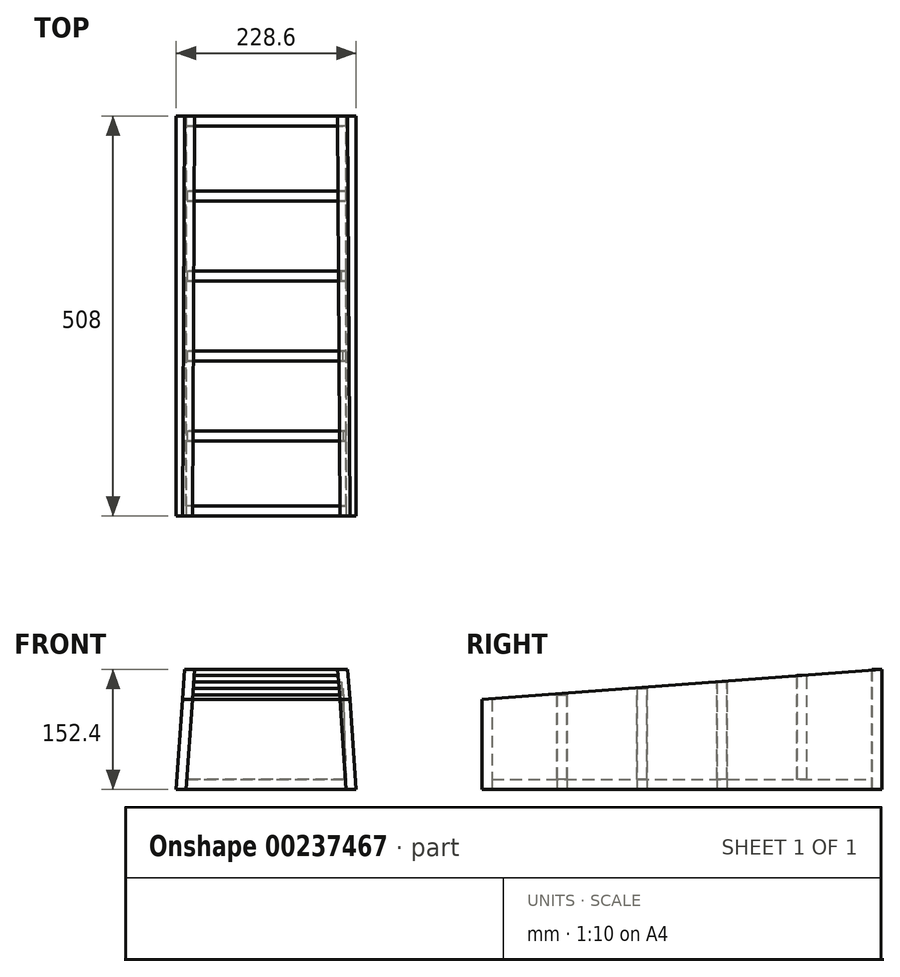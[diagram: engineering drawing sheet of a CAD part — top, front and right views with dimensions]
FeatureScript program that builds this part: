
annotation { "Feature Type Name" : "Feature", "Feature Type Description" : "" }
export const myFeature = defineFeature(function(context is Context, id is Id, definition is map)
    precondition{}
    {
        {
            var Q0;
            Q0=qCreatedBy(makeId("Right.planeOp"),FACE);
            var sketch = newSketch(context, id + "F0", { "sketchPlane" : qUnion([Q0])});
            skLineSegment(sketch, "E0", {"start": v(0, 0) * mm, "end": v(0, 152.4) * mm});
            skLineSegment(sketch, "E1", {"start": v(0, 152.4) * mm, "end": v(-508, 114.3) * mm});
            skLineSegment(sketch, "E2", {"start": v(-508, 114.3) * mm, "end": v(-508, 0) * mm});
            skLineSegment(sketch, "E3", {"start": v(-508, 0) * mm, "end": v(0, 0) * mm});
            skSolve(sketch);
        }
        {
            var Q0;
            Q0=makeQuery(id+"F0.imprint","IMPRINT",FACE,{"disambiguationData":[TD([[makeQuery(id+"F0.imprint","IMPRINT",EDGE,{"derivedFrom":sQuery(id+"F0.wireOp",EDGE,"E0")}),1.0]])]});
            extrude(context, id + "F1", {"entities" : qUnion([Q0]), "oppositeDirection" : true, "depth" : 114.3 * mm});
        }
        {
            var Q0;
            Q0=qCreatedBy(makeId("Front.planeOp"),FACE);
            var sketch = newSketch(context, id + "F2", { "sketchPlane" : qUnion([Q0])});
            skLineSegment(sketch, "E4", {"start": v(-114.3, 0) * mm, "end": v(-103.46, 155.08) * mm});
            skLineSegment(sketch, "E5", {"start": v(-103.46, 155.08) * mm, "end": v(-133.17, 155.08) * mm});
            skLineSegment(sketch, "E6", {"start": v(-133.17, 155.08) * mm, "end": v(-133.17, 0) * mm});
            skLineSegment(sketch, "E7", {"start": v(-133.17, 0) * mm, "end": v(-114.3, 0) * mm});
            skSolve(sketch);
        }
        {
            var Q0;
            Q0=makeQuery(id+"F2.imprint","IMPRINT",FACE,{"disambiguationData":[TD([[makeQuery(id+"F2.imprint","IMPRINT",EDGE,{"derivedFrom":sQuery(id+"F2.wireOp",EDGE,"E4")}),1.0]])]});
            var Q1;
            Q1=makeQuery(id+"F1.opExtrude","SWEPT_BODY",BODY,{"disambiguationData":[OSD([sQuery(id+"F0.wireOp",EDGE,"E0"),sQuery(id+"F0.wireOp",EDGE,"E1"),sQuery(id+"F0.wireOp",EDGE,"E2"),sQuery(id+"F0.wireOp",EDGE,"E3")])]});
            extrude(context, id + "F3", {"entities" : qUnion([Q0]), "operationType" : NewBodyOperationType.REMOVE, "endBoundEntityBody" : qUnion([Q1]), "depth" : 528.32 * mm});
        }
        {
            var Q0;
            Q0=qCreatedBy(makeId("Front.planeOp"),FACE);
            var sketch = newSketch(context, id + "F4", { "sketchPlane" : qUnion([Q0])});
            skLineSegment(sketch, "E8", {"start": v(-90.18, 162.83) * mm, "end": v(-102.71, -16.34) * mm});
            skLineSegment(sketch, "E9", {"start": v(-102.71, -16.34) * mm, "end": v(0, -16.34) * mm});
            skLineSegment(sketch, "E10", {"start": v(0, -16.34) * mm, "end": v(0, 168.36) * mm});
            skLineSegment(sketch, "E11", {"start": v(0, 168.36) * mm, "end": v(-90.18, 162.83) * mm});
            skSolve(sketch);
        }
        {
            var Q0;
            Q0=makeQuery(id+"F4.imprint","IMPRINT",FACE,{"disambiguationData":[TD([[makeQuery(id+"F4.imprint","IMPRINT",EDGE,{"derivedFrom":sQuery(id+"F4.wireOp",EDGE,"E8")}),1.0]])]});
            extrude(context, id + "F5", {"entities" : qUnion([Q0]), "operationType" : NewBodyOperationType.REMOVE, "depth" : 508 * mm});
        }
        {
            var Q0;
            Q0=makeQuery(id+"F1.opExtrude","SWEPT_BODY",BODY,{"disambiguationData":[OSD([sQuery(id+"F0.wireOp",EDGE,"E0"),sQuery(id+"F0.wireOp",EDGE,"E1"),sQuery(id+"F0.wireOp",EDGE,"E2"),sQuery(id+"F0.wireOp",EDGE,"E3")])]});
            var Q1;
            Q1=qCreatedBy(makeId("Right.planeOp"),FACE);
            mirror(context, id + "F6", {"entities" : qUnion([Q0]), "mirrorPlane" : qUnion([Q1])});
        }
        {
            var Q0;
            Q0=makeQuery(id+"F1.opExtrude","SWEPT_FACE",FACE,{"disambiguationData":[OSD([sQuery(id+"F0.wireOp",EDGE,"E0")])]});
            var sketch = newSketch(context, id + "F7", { "sketchPlane" : qUnion([Q0])});
            skLineSegment(sketch, "E12", {"start": v(-90.91, 152.4) * mm, "end": v(90.91, 152.4) * mm});
            skLineSegment(sketch, "E13", {"start": v(90.91, 152.4) * mm, "end": v(101.57, 0) * mm});
            skLineSegment(sketch, "E14", {"start": v(101.57, 0) * mm, "end": v(-101.57, 0) * mm});
            skLineSegment(sketch, "E15", {"start": v(-101.57, 0) * mm, "end": v(-90.91, 152.4) * mm});
            skSolve(sketch);
        }
        {
            var Q0;
            Q0=makeQuery(id+"F7.imprint","IMPRINT",FACE,{"disambiguationData":[TD([[makeQuery(id+"F7.imprint","IMPRINT",EDGE,{"derivedFrom":sQuery(id+"F7.wireOp",EDGE,"E12")}),-1.0]])]});
            extrude(context, id + "F8", {"entities" : qUnion([Q0]), "oppositeDirection" : true, "depth" : 12.7 * mm});
        }
        {
            var Q0;
            Q0=makeQuery(id+"F1.opExtrude","SWEPT_FACE",FACE,{"disambiguationData":[OSD([sQuery(id+"F0.wireOp",EDGE,"E2")])]});
            var sketch = newSketch(context, id + "F9", { "sketchPlane" : qUnion([Q0])});
            skPoint(sketch, "E16.end.orphan", {"position": v(101.57, 0) * mm});
            skLineSegment(sketch, "E17", {"start": v(-101.57, 0) * mm, "end": v(-93.58, 114.3) * mm});
            skLineSegment(sketch, "E18", {"start": v(-93.58, 114.3) * mm, "end": v(93.58, 114.3) * mm});
            skLineSegment(sketch, "E19", {"start": v(93.58, 114.3) * mm, "end": v(101.57, 0) * mm});
            skLineSegment(sketch, "E20", {"start": v(101.57, 0) * mm, "end": v(-101.57, 0) * mm});
            skSolve(sketch);
        }
        {
            var Q0;
            Q0=qCreatedBy(makeId("Front.planeOp"),FACE);
            cPlane(context, id + "F10", {"entities" : qUnion([Q0]), "cplaneType" : CPlaneType.OFFSET, "offset" : 101.6 * mm, "width" : 152.4 * mm, "height" : 152.4 * mm});
        }
        {
            var Q0;
            Q0=qCreatedBy(makeId("Front.planeOp"),FACE);
            cPlane(context, id + "F11", {"entities" : qUnion([Q0]), "cplaneType" : CPlaneType.OFFSET, "offset" : 203.2 * mm, "width" : 152.4 * mm, "height" : 152.4 * mm});
        }
        {
            var Q0;
            Q0=qCreatedBy(makeId("Front.planeOp"),FACE);
            cPlane(context, id + "F12", {"entities" : qUnion([Q0]), "cplaneType" : CPlaneType.OFFSET, "offset" : 304.8 * mm, "width" : 152.4 * mm, "height" : 152.4 * mm});
        }
        {
            var Q0;
            Q0=qCreatedBy(id+"F10.planeOp",FACE);
            var sketch = newSketch(context, id + "F13", { "sketchPlane" : qUnion([Q0])});
            skLineSegment(sketch, "E21", {"start": v(-101.57, 0) * mm, "end": v(-91.44, 144.78) * mm});
            skLineSegment(sketch, "E22", {"start": v(-91.44, 144.78) * mm, "end": v(91.44, 144.78) * mm});
            skLineSegment(sketch, "E23", {"start": v(91.44, 144.78) * mm, "end": v(101.57, 0) * mm});
            skLineSegment(sketch, "E24", {"start": v(101.57, 0) * mm, "end": v(-101.57, 0) * mm});
            skSolve(sketch);
        }
        {
            var Q0;
            Q0=makeQuery(id+"F13.imprint","IMPRINT",FACE,{"disambiguationData":[TD([[makeQuery(id+"F13.imprint","IMPRINT",EDGE,{"derivedFrom":sQuery(id+"F13.wireOp",EDGE,"E21")}),-1.0]])]});
            extrude(context, id + "F14", {"entities" : qUnion([Q0]), "depth" : 6.35 * mm, "hasSecondDirection" : true, "secondDirectionOppositeDirection" : true, "secondDirectionDepth" : 6.35 * mm});
        }
        {
            var Q0;
            Q0=qCreatedBy(id+"F11.planeOp",FACE);
            var sketch = newSketch(context, id + "F15", { "sketchPlane" : qUnion([Q0])});
            skLineSegment(sketch, "E25", {"start": v(-101.57, 0) * mm, "end": v(-92.03, 136.36) * mm});
            skLineSegment(sketch, "E26", {"start": v(-92.03, 136.36) * mm, "end": v(96, 136.36) * mm});
            skLineSegment(sketch, "E27", {"start": v(96, 136.36) * mm, "end": v(101.57, 0) * mm});
            skLineSegment(sketch, "E28", {"start": v(101.57, 0) * mm, "end": v(-101.57, 0) * mm});
            skSolve(sketch);
        }
        {
            var Q0;
            Q0=makeQuery(id+"F15.imprint","IMPRINT",FACE,{"disambiguationData":[TD([[makeQuery(id+"F15.imprint","IMPRINT",EDGE,{"derivedFrom":sQuery(id+"F15.wireOp",EDGE,"E25")}),-1.0]])]});
            extrude(context, id + "F16", {"entities" : qUnion([Q0]), "depth" : 6.35 * mm, "hasSecondDirection" : true, "secondDirectionOppositeDirection" : true, "secondDirectionDepth" : 6.35 * mm});
        }
        {
            var Q0;
            Q0=qCreatedBy(id+"F12.planeOp",FACE);
            var sketch = newSketch(context, id + "F17", { "sketchPlane" : qUnion([Q0])});
            skLineSegment(sketch, "E29", {"start": v(-101.57, 0) * mm, "end": v(-92.58, 128.53) * mm});
            skLineSegment(sketch, "E30", {"start": v(-92.58, 128.53) * mm, "end": v(97.61, 128.53) * mm});
            skLineSegment(sketch, "E31", {"start": v(97.61, 128.53) * mm, "end": v(101.57, 0) * mm});
            skLineSegment(sketch, "E32", {"start": v(101.57, 0) * mm, "end": v(-101.57, 0) * mm});
            skSolve(sketch);
        }
        {
            var Q0;
            Q0=makeQuery(id+"F17.imprint","IMPRINT",FACE,{"disambiguationData":[TD([[makeQuery(id+"F17.imprint","IMPRINT",EDGE,{"derivedFrom":sQuery(id+"F17.wireOp",EDGE,"E29")}),-1.0]])]});
            extrude(context, id + "F18", {"entities" : qUnion([Q0]), "depth" : 6.35 * mm, "hasSecondDirection" : true, "secondDirectionOppositeDirection" : true, "secondDirectionDepth" : 6.35 * mm});
        }
        {
            var Q0;
            Q0=qCreatedBy(makeId("Front.planeOp"),FACE);
            cPlane(context, id + "F19", {"entities" : qUnion([Q0]), "cplaneType" : CPlaneType.OFFSET, "offset" : 406.4 * mm, "width" : 152.4 * mm, "height" : 152.4 * mm});
        }
        {
            var Q0;
            Q0=qCreatedBy(id+"F19.planeOp",FACE);
            var sketch = newSketch(context, id + "F20", { "sketchPlane" : qUnion([Q0])});
            skLineSegment(sketch, "E33", {"start": v(-101.57, 0) * mm, "end": v(-93.16, 120.3) * mm});
            skLineSegment(sketch, "E34", {"start": v(-93.16, 120.3) * mm, "end": v(98.1, 120.3) * mm});
            skLineSegment(sketch, "E35", {"start": v(98.1, 120.3) * mm, "end": v(101.57, 0) * mm});
            skLineSegment(sketch, "E36", {"start": v(101.57, 0) * mm, "end": v(-101.57, 0) * mm});
            skSolve(sketch);
        }
        {
            var Q0;
            Q0=makeQuery(id+"F20.imprint","IMPRINT",FACE,{"disambiguationData":[TD([[makeQuery(id+"F20.imprint","IMPRINT",EDGE,{"derivedFrom":sQuery(id+"F20.wireOp",EDGE,"E33")}),-1.0]])]});
            extrude(context, id + "F21", {"entities" : qUnion([Q0]), "depth" : 6.35 * mm, "hasSecondDirection" : true, "secondDirectionOppositeDirection" : true, "secondDirectionDepth" : 6.35 * mm});
        }
        {
            var Q0;
            Q0=makeQuery(id+"F9.imprint","IMPRINT",FACE,{"disambiguationData":[TD([[makeQuery(id+"F9.imprint","IMPRINT",EDGE,{"derivedFrom":sQuery(id+"F9.wireOp",EDGE,"E17")}),1.0]])]});
            extrude(context, id + "F22", {"entities" : qUnion([Q0]), "oppositeDirection" : true, "depth" : 12.7 * mm});
        }
        {
            var Q0;
            Q0=makeQuery(id+"F22.opExtrude","CAP_FACE",FACE,{"disambiguationData":[OSD([sQuery(id+"F9.wireOp",EDGE,"E17"),sQuery(id+"F9.wireOp",EDGE,"E18"),sQuery(id+"F9.wireOp",EDGE,"E19"),sQuery(id+"F9.wireOp",EDGE,"E20")])],"isStart":false});
            var sketch = newSketch(context, id + "F23", { "sketchPlane" : qUnion([Q0])});
            skLineSegment(sketch, "E37", {"start": v(-101.57, 0) * mm, "end": v(-100.68, 12.7) * mm});
            skLineSegment(sketch, "E38", {"start": v(-100.68, 12.7) * mm, "end": v(100.68, 12.7) * mm});
            skLineSegment(sketch, "E39", {"start": v(100.68, 12.7) * mm, "end": v(101.57, 0) * mm});
            skLineSegment(sketch, "E40", {"start": v(101.57, 0) * mm, "end": v(-101.57, 0) * mm});
            skSolve(sketch);
        }
        {
            var Q0;
            Q0=makeQuery(id+"F23.imprint","IMPRINT",FACE,{"disambiguationData":[TD([[makeQuery(id+"F23.imprint","IMPRINT",EDGE,{"derivedFrom":sQuery(id+"F23.wireOp",EDGE,"E37")}),1.0]])]});
            var Q1;
            Q1=makeQuery(id+"F8.opExtrude","CAP_FACE",FACE,{"disambiguationData":[OSD([sQuery(id+"F7.wireOp",EDGE,"E12"),sQuery(id+"F7.wireOp",EDGE,"E13"),sQuery(id+"F7.wireOp",EDGE,"E14"),sQuery(id+"F7.wireOp",EDGE,"E15")])],"isStart":false});
            extrude(context, id + "F24", {"entities" : qUnion([Q0]), "operationType" : NewBodyOperationType.REMOVE, "endBound" : BoundingType.UP_TO_SURFACE, "endBoundEntityFace" : qUnion([Q1]), "depth" : 25.4 * mm});
        }
        {
            var Q0;
            Q0=qCreatedBy(makeId("Top.planeOp"),FACE);
            var sketch = newSketch(context, id + "F25", { "sketchPlane" : qUnion([Q0])});
            skLineSegment(sketch, "E41.bottom", {"start": v(-101.57, -495.3) * mm, "end": v(101.57, -495.3) * mm});
            skLineSegment(sketch, "E41.top", {"start": v(-101.57, -12.7) * mm, "end": v(101.57, -12.7) * mm});
            skLineSegment(sketch, "E41.left", {"start": v(-101.57, -495.3) * mm, "end": v(-101.57, -12.7) * mm});
            skLineSegment(sketch, "E41.right", {"start": v(101.57, -495.3) * mm, "end": v(101.57, -12.7) * mm});
            skSolve(sketch);
        }
        {
            var Q0;
            Q0=makeQuery(id+"F25.imprint","IMPRINT",FACE,{"disambiguationData":[TD([[makeQuery(id+"F25.imprint","IMPRINT",EDGE,{"derivedFrom":sQuery(id+"F25.wireOp",EDGE,"E41.bottom")}),1.0]])]});
            extrude(context, id + "F26", {"entities" : qUnion([Q0]), "depth" : 12.7 * mm});
        }
    });
